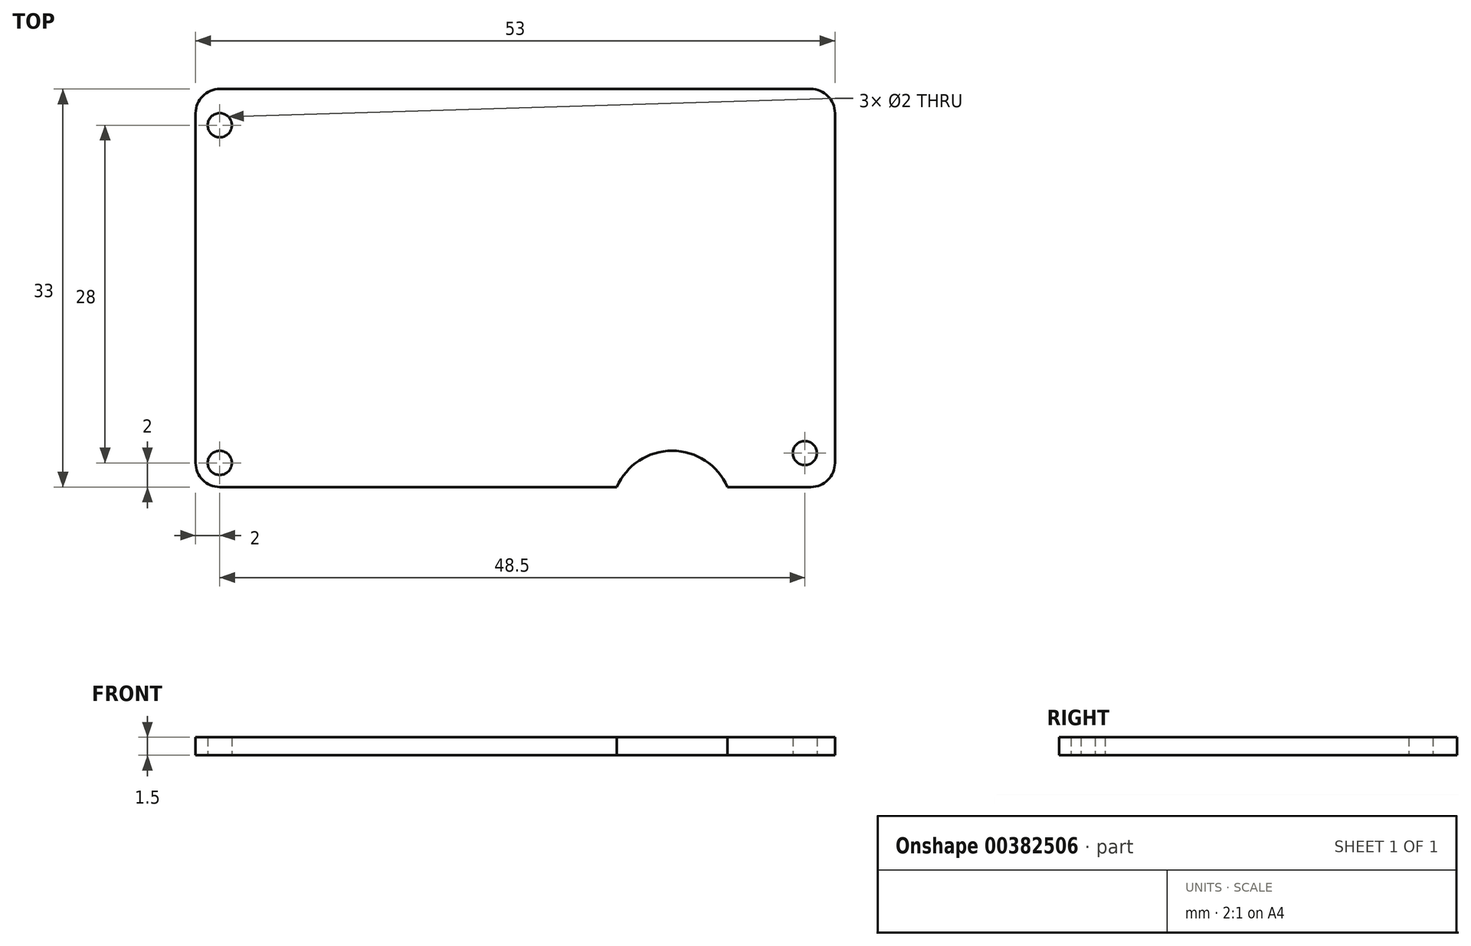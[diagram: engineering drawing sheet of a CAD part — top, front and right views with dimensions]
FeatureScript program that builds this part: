
annotation { "Feature Type Name" : "Feature", "Feature Type Description" : "" }
export const myFeature = defineFeature(function(context is Context, id is Id, definition is map)
    precondition{}
    {
        {
            var Q0;
            Q0=qCreatedBy(makeId("Top.planeOp"),FACE);
            var sketch = newSketch(context, id + "F0", { "sketchPlane" : qUnion([Q0])});
            skLineSegment(sketch, "E0.bottom", {"start": v(26.5, 16.5) * mm, "end": v(-26.5, 16.5) * mm});
            skLineSegment(sketch, "E0.top", {"start": v(26.5, -16.5) * mm, "end": v(-26.5, -16.5) * mm});
            skLineSegment(sketch, "E0.left", {"start": v(26.5, 16.5) * mm, "end": v(26.5, -16.5) * mm});
            skLineSegment(sketch, "E0.right", {"start": v(-26.5, 16.5) * mm, "end": v(-26.5, -16.5) * mm});
            skPoint(sketch, "E0.middle", {"position": v(0, 0) * mm});
            skCircle(sketch, "E1", {"center": v(-24.5, 13.5) * mm, "radius": 1 * mm});
            skCircle(sketch, "E2", {"center": v(-24.5, -14.5) * mm, "radius": 1 * mm});
            skCircle(sketch, "E3", {"center": v(24, -13.69) * mm, "radius": 1 * mm});
            skCircle(sketch, "E4", {"center": v(13, -18.5) * mm, "radius": 5 * mm});
            skSolve(sketch);
        }
        {
            var Q0;
            Q0=makeQuery(id+"F0.imprint","IMPRINT",FACE,{"disambiguationData":[TD([[makeQuery(id+"F0.imprint","IMPRINT",EDGE,{"derivedFrom":sQuery(id+"F0.wireOp",EDGE,"E0.bottom")}),1.0]])]});
            extrude(context, id + "F1", {"entities" : qUnion([Q0]), "depth" : 1.5 * mm});
        }
        {
            var Q0;
            Q0=makeQuery(id+"F1.opExtrude","SWEPT_EDGE",EDGE,{"disambiguationData":[OSD([sQuery(id+"F0.wireOp",EDGE,"E0.top"),sQuery(id+"F0.wireOp",EDGE,"E0.right")])]});
            var Q1;
            Q1=makeQuery(id+"F1.opExtrude","SWEPT_EDGE",EDGE,{"disambiguationData":[OSD([sQuery(id+"F0.wireOp",EDGE,"E0.top"),sQuery(id+"F0.wireOp",EDGE,"E0.left")])]});
            var Q2;
            Q2=makeQuery(id+"F1.opExtrude","SWEPT_EDGE",EDGE,{"disambiguationData":[OSD([sQuery(id+"F0.wireOp",EDGE,"E0.bottom"),sQuery(id+"F0.wireOp",EDGE,"E0.left")])]});
            var Q3;
            Q3=makeQuery(id+"F1.opExtrude","SWEPT_EDGE",EDGE,{"disambiguationData":[OSD([sQuery(id+"F0.wireOp",EDGE,"E0.bottom"),sQuery(id+"F0.wireOp",EDGE,"E0.right")])]});
            fillet(context, id + "F2", {"entities" : qUnion([Q0, Q1, Q2, Q3]), "radius" : 2 * mm, "tangentPropagation" : true, "allowEdgeOverflow" : false});
        }
    });
